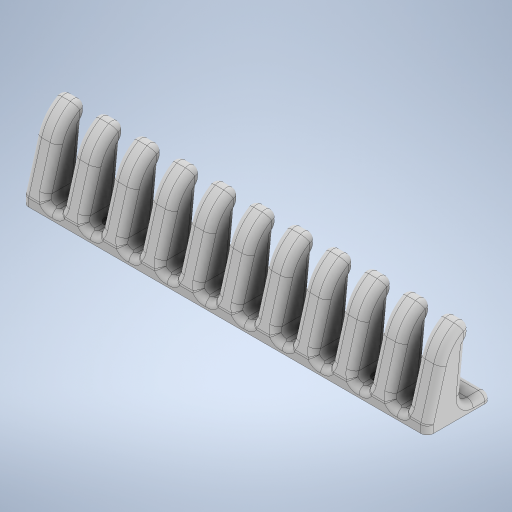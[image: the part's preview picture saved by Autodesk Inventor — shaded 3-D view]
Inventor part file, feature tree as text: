
AUTODESK INVENTOR PART (.ipt)
format: ipt  version: 2023 (Build 270158030, 158C)  size: 1,214,976 bytes
history: native  units: mm
features: fillet x10, sketch x4, extrude x3, hole x1
ambient origin geometry x8: Origin, YZ Plane, XZ Plane, XY Plane, X Axis, Y Axis, Z Axis, Center Point
bodies: Solid1 (feature_tree)
feature tree (18):
  extrude  "Extrusion1"  Depth=190.0mm
  extrude  "Extrusion2"  Depth=4.0mm
  extrude  "Extrusion3"  Depth=10.0mm
  fillet  "Fillet1"  Radius=190.0mm
  fillet  "Fillet3"  Radius=35.0mm
  fillet  "Fillet6"  Radius=10.0mm
  fillet  "Fillet10"  Radius=16.0mm
  fillet  "Fillet11"  [1 undecoded]
  fillet  "Fillet12"  Radius=5.0mm
  fillet  "Fillet13"  Radius=20.0mm
  fillet  "Fillet14"  Radius=3.0mm
  fillet  "Fillet15"  Radius=3.0mm
  fillet  "Fillet16"  Radius=3.0mm
  hole  "Hole1"  [1 undecoded]
  sketch  "Sketch1"  dims[d0=30.0mm d1=190.0mm]
  sketch  "Sketch2"  dims[d2=4.0mm d3=0.0mm d4=20.0mm]
  sketch  "Sketch3"  dims[d5=10.0mm d18=110.0mm d20=18.0mm d21=10.0mm d23=10.0mm d25=190.0mm d26=35.0mm d27=0.0mm d28=10.0mm d29=16.0mm d30=0.0mm d31=0.0mm d32=5.0mm d34=20.0mm d37=3.0mm d41=3.0mm d42=3.0mm]
  sketch  "Sketch4"  dims[d43=3.0mm d44=3.0mm d45=3.0mm d46=3.0mm d47=3.0mm d48=3.0mm d49=9.0mm d50=4.0mm d51=4.0mm d52=4.0mm d53=4.0mm d54=24.2mm d55=3.242mm d56=8.0mm d57=5.0mm d58=1.0mm d59=90.0deg d60=8.0mm d61=20.594885mm d62=29.0mm d63=30.0mm d64=1.0mm d65=0.0mm d66=0.0mm d67=0.0mm d68=0.0mm]
note: 2 required parameter values undecoded (feature->parameter linkage not recoverable at this tier; creation-order binding heuristic only, values carry confidence <= 0.55)
